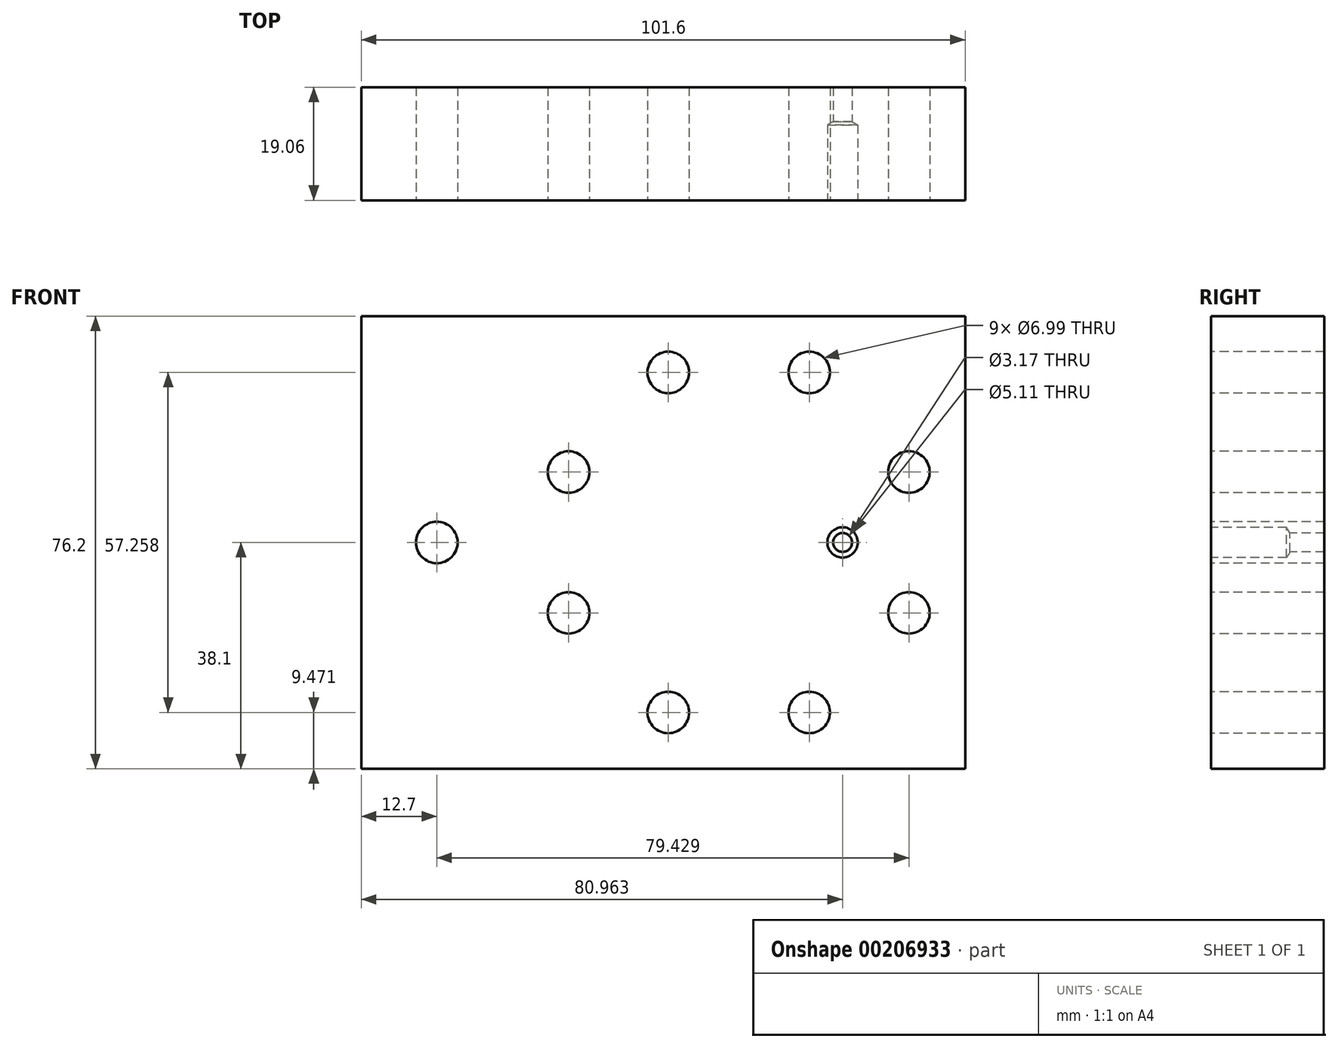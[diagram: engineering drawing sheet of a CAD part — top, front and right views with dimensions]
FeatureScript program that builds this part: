
annotation { "Feature Type Name" : "Feature", "Feature Type Description" : "" }
export const myFeature = defineFeature(function(context is Context, id is Id, definition is map)
    precondition{}
    {
        {
            var Q0;
            Q0=qCreatedBy(makeId("Front.planeOp"),FACE);
            var sketch = newSketch(context, id + "F0", { "sketchPlane" : qUnion([Q0])});
            skLineSegment(sketch, "E0.bottom", {"start": v(-63.5, 38.1) * mm, "end": v(38.1, 38.1) * mm});
            skLineSegment(sketch, "E0.top", {"start": v(-63.5, -38.1) * mm, "end": v(38.1, -38.1) * mm});
            skLineSegment(sketch, "E0.left", {"start": v(-63.5, 38.1) * mm, "end": v(-63.5, -38.1) * mm});
            skLineSegment(sketch, "E0.right", {"start": v(38.1, 38.1) * mm, "end": v(38.1, -38.1) * mm});
            skSolve(sketch);
        }
        {
            var Q0;
            Q0 = qSketchRegion(id + "F0", true);
            extrude(context, id + "F1", {"entities" : qUnion([Q0]), "endBound" : BoundingType.SYMMETRIC, "depth" : 19.05 * mm});
        }
        {
            var Q0;
            Q0=makeQuery(id+"F1.opExtrude","CAP_FACE",FACE,{"disambiguationData":[OSD([sQuery(id+"F0.wireOp",EDGE,"E0.bottom"),sQuery(id+"F0.wireOp",EDGE,"E0.top"),sQuery(id+"F0.wireOp",EDGE,"E0.left"),sQuery(id+"F0.wireOp",EDGE,"E0.right")])],"isStart":false});
            var sketch = newSketch(context, id + "F2", { "sketchPlane" : qUnion([Q0])});
            skLineSegment(sketch, "E1", {"start": v(0, 0) * mm, "end": v(11.86, 28.63) * mm, "construction": true});
            skCircle(sketch, "E2", {"center": v(11.86, 28.63) * mm, "radius": 3.5 * mm});
            skCircle(sketch, "E3.1.0", {"center": v(-11.86, 28.63) * mm, "radius": 3.5 * mm});
            skCircle(sketch, "E3.2.0", {"center": v(-28.63, 11.86) * mm, "radius": 3.5 * mm});
            skCircle(sketch, "E3.3.0", {"center": v(-28.63, -11.86) * mm, "radius": 3.5 * mm});
            skCircle(sketch, "E3.4.0", {"center": v(-11.86, -28.63) * mm, "radius": 3.5 * mm});
            skCircle(sketch, "E3.5.0", {"center": v(11.86, -28.63) * mm, "radius": 3.5 * mm});
            skCircle(sketch, "E3.6.0", {"center": v(28.63, -11.86) * mm, "radius": 3.5 * mm});
            skCircle(sketch, "E3.7.0", {"center": v(28.63, 11.86) * mm, "radius": 3.5 * mm});
            skPoint(sketch, "E3.center", {"position": v(0, 0) * mm});
            skSolve(sketch);
        }
        {
            var Q0;
            Q0 = qSketchRegion(id + "F2", true);
            extrude(context, id + "F3", {"entities" : qUnion([Q0]), "operationType" : NewBodyOperationType.REMOVE, "oppositeDirection" : true, "depth" : 25.4 * mm});
        }
        {
            var Q0;
            Q0=makeQuery(id+"F1.opExtrude","CAP_FACE",FACE,{"disambiguationData":[OSD([sQuery(id+"F0.wireOp",EDGE,"E0.bottom"),sQuery(id+"F0.wireOp",EDGE,"E0.top"),sQuery(id+"F0.wireOp",EDGE,"E0.left"),sQuery(id+"F0.wireOp",EDGE,"E0.right")])],"isStart":false});
            var sketch = newSketch(context, id + "F4", { "sketchPlane" : qUnion([Q0])});
            skCircle(sketch, "E4", {"center": v(-50.8, 0) * mm, "radius": 3.5 * mm});
            skSolve(sketch);
        }
        {
            var Q0;
            Q0 = qSketchRegion(id + "F4", true);
            extrude(context, id + "F5", {"entities" : qUnion([Q0]), "operationType" : NewBodyOperationType.REMOVE, "oppositeDirection" : true, "depth" : 25.4 * mm});
        }
        {
            var Q0;
            Q0=makeQuery(id+"F1.opExtrude","CAP_FACE",FACE,{"disambiguationData":[OSD([sQuery(id+"F0.wireOp",EDGE,"E0.bottom"),sQuery(id+"F0.wireOp",EDGE,"E0.top"),sQuery(id+"F0.wireOp",EDGE,"E0.left"),sQuery(id+"F0.wireOp",EDGE,"E0.right")])],"isStart":false});
            var sketch = newSketch(context, id + "F6", { "sketchPlane" : qUnion([Q0])});
            skCircle(sketch, "E5", {"center": v(17.46, 0) * mm, "radius": 1.59 * mm});
            skCircle(sketch, "E6", {"center": v(0, 0) * mm, "radius": 19.05 * mm, "construction": true});
            skSolve(sketch);
        }
        {
            var Q0;
            Q0 = qSketchRegion(id + "F6", true);
            extrude(context, id + "F7", {"entities" : qUnion([Q0]), "operationType" : NewBodyOperationType.REMOVE, "oppositeDirection" : true, "depth" : 25.4 * mm});
        }
        {
            var Q0;
            Q0=makeQuery(id+"F1.opExtrude","CAP_FACE",FACE,{"disambiguationData":[OSD([sQuery(id+"F0.wireOp",EDGE,"E0.bottom"),sQuery(id+"F0.wireOp",EDGE,"E0.top"),sQuery(id+"F0.wireOp",EDGE,"E0.left"),sQuery(id+"F0.wireOp",EDGE,"E0.right")])],"isStart":false});
            var sketch = newSketch(context, id + "F8", { "sketchPlane" : qUnion([Q0])});
            skCircle(sketch, "E7", {"center": v(17.46, 0) * mm, "radius": 3.18 * mm, "construction": true});
            skSolve(sketch);
        }
        {
            var Q0;
            Q0=sQuery(id+"F8.wireOp",VERTEX,"E7.center");
            var Q1;
            Q1=makeQuery(id+"F1.opExtrude","SWEPT_BODY",BODY,{"disambiguationData":[OSD([sQuery(id+"F0.wireOp",EDGE,"E0.bottom"),sQuery(id+"F0.wireOp",EDGE,"E0.top"),sQuery(id+"F0.wireOp",EDGE,"E0.left"),sQuery(id+"F0.wireOp",EDGE,"E0.right")])]});
            hole(context, id + "F9", {"style" : HoleStyle.SIMPLE, "endStyle" : HoleEndStyle.BLIND, "standardTappedOrClearance" : lookupTablePath({ "standard" : "ANSI", "engagement" : "75%", "pitch" : "20 tpi", "size" : "1/4", "type" : "Tapped" }), "standardBlindInLast" : lookupTablePath({ "standard" : "ANSI", "engagement" : "75%", "pitch" : "20 tpi", "size" : "1/4", "type" : "Tapped" }), "holeDiameter" : 5.1 * mm, "holeDepth" : 12.7 * mm, "locations" : qUnion([Q0]), "scope" : qUnion([Q1]), "majorDiameter" : 6.35 * mm});
        }
    });
